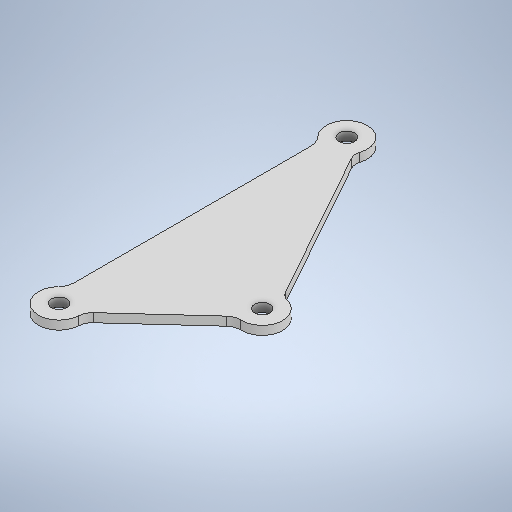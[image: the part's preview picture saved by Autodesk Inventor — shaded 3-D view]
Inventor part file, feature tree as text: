
AUTODESK INVENTOR PART (.ipt)
format: ipt  version: 2025.2 (Build 292293000, 293)  size: 313,344 bytes
history: native  units: in
note: dims shown in document units (in); Inventor stores cm internally (conversion verified against a paired STEP export)
features: extrude x4, sketch x3
ambient origin geometry x8: Origin, YZ Plane, XZ Plane, XY Plane, X Axis, Y Axis, Z Axis, Center Point
bodies: Solid1 (feature_tree)
feature tree (7):
  sketch  "Sketch1"  dims[d0=0.315in d1=0.315in]
  extrude  "Extrusion1"  Depth=0.315in
  extrude  "Extrusion2"  Depth=1.6732in
  extrude  "Extrusion3"  Depth=2.2059in
  extrude  "Extrusion4"  Depth=2.2059in
  sketch  "Sketch2"  dims[d2=0.315in d4=1.6732in]
  sketch  "Sketch3"  dims[d5=1.1024in d6=0.0787in d7=0.0787in d8=0.1969in d10=0.1969in d11=0.0in d12=0.2066in d14=0.2066in d15=0.0787in d16=0.0787in d17=0.0787in d18=0.0787in d19=0.1575in d20=0.1969in d21=0.1969in d22=0.1969in d23=0.0433in d24=0.0521in d25=0.1575in d26=0.0in d27=0.0669in d28=0.0in d29=0.1181in d30=0.1181in d31=0.1181in d32=0.1575in d33=0.0in d34=3.937in d35=0.0in d36=0.0in d38=2.2059in]
